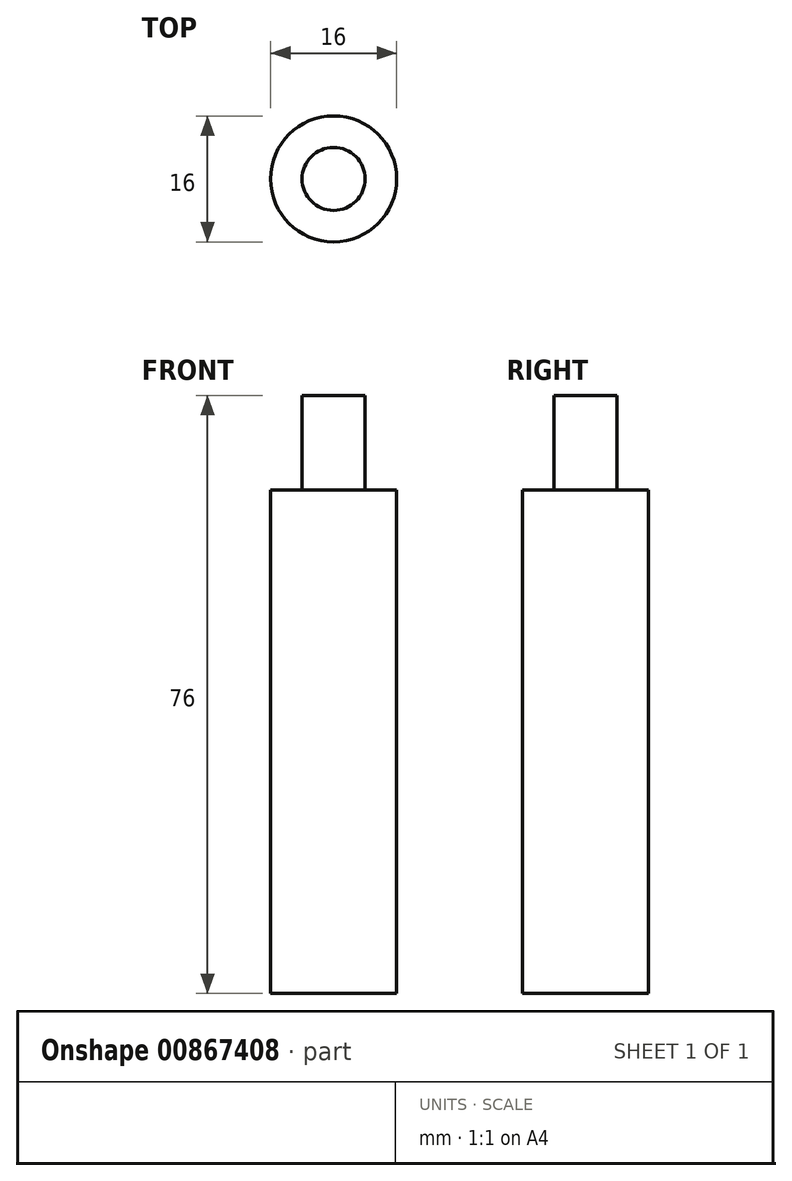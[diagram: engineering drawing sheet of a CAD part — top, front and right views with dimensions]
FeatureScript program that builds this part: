
annotation { "Feature Type Name" : "Feature", "Feature Type Description" : "" }
export const myFeature = defineFeature(function(context is Context, id is Id, definition is map)
    precondition{}
    {
        {
            var Q0;
            Q0=qCreatedBy(makeId("Top.planeOp"),FACE);
            var sketch = newSketch(context, id + "F0", { "sketchPlane" : qUnion([Q0])});
            skCircle(sketch, "E0", {"center": v(0, 0) * mm, "radius": 8 * mm});
            skSolve(sketch);
        }
        {
            var Q0;
            Q0=makeQuery(id+"F0.imprint","IMPRINT",FACE,{"disambiguationData":[TD([[makeQuery(id+"F0.imprint","IMPRINT",EDGE,{"derivedFrom":sQuery(id+"F0.wireOp",EDGE,"E0")}),1.0]])]});
            extrude(context, id + "F1", {"entities" : qUnion([Q0]), "depth" : 76 * mm, "offsetDistance" : 25 * mm});
        }
        {
            var Q0;
            Q0=makeQuery(id+"F1.opExtrude","CAP_FACE",FACE,{"disambiguationData":[OSD([sQuery(id+"F0.wireOp",EDGE,"E0")])],"isStart":false});
            var sketch = newSketch(context, id + "F2", { "sketchPlane" : qUnion([Q0])});
            skCircle(sketch, "E1.0", {"center": v(0, 0) * mm, "radius": 4 * mm});
            skCircle(sketch, "E2.0", {"center": v(0, 0) * mm, "radius": 8 * mm});
            skSolve(sketch);
        }
        {
            var Q0;
            Q0=qSketchRegion(id+"F2",true);
            extrude(context, id + "F3", {"entities" : qUnion([Q0]), "operationType" : NewBodyOperationType.REMOVE, "oppositeDirection" : true, "depth" : 12 * mm, "offsetDistance" : 25 * mm});
        }
    });
